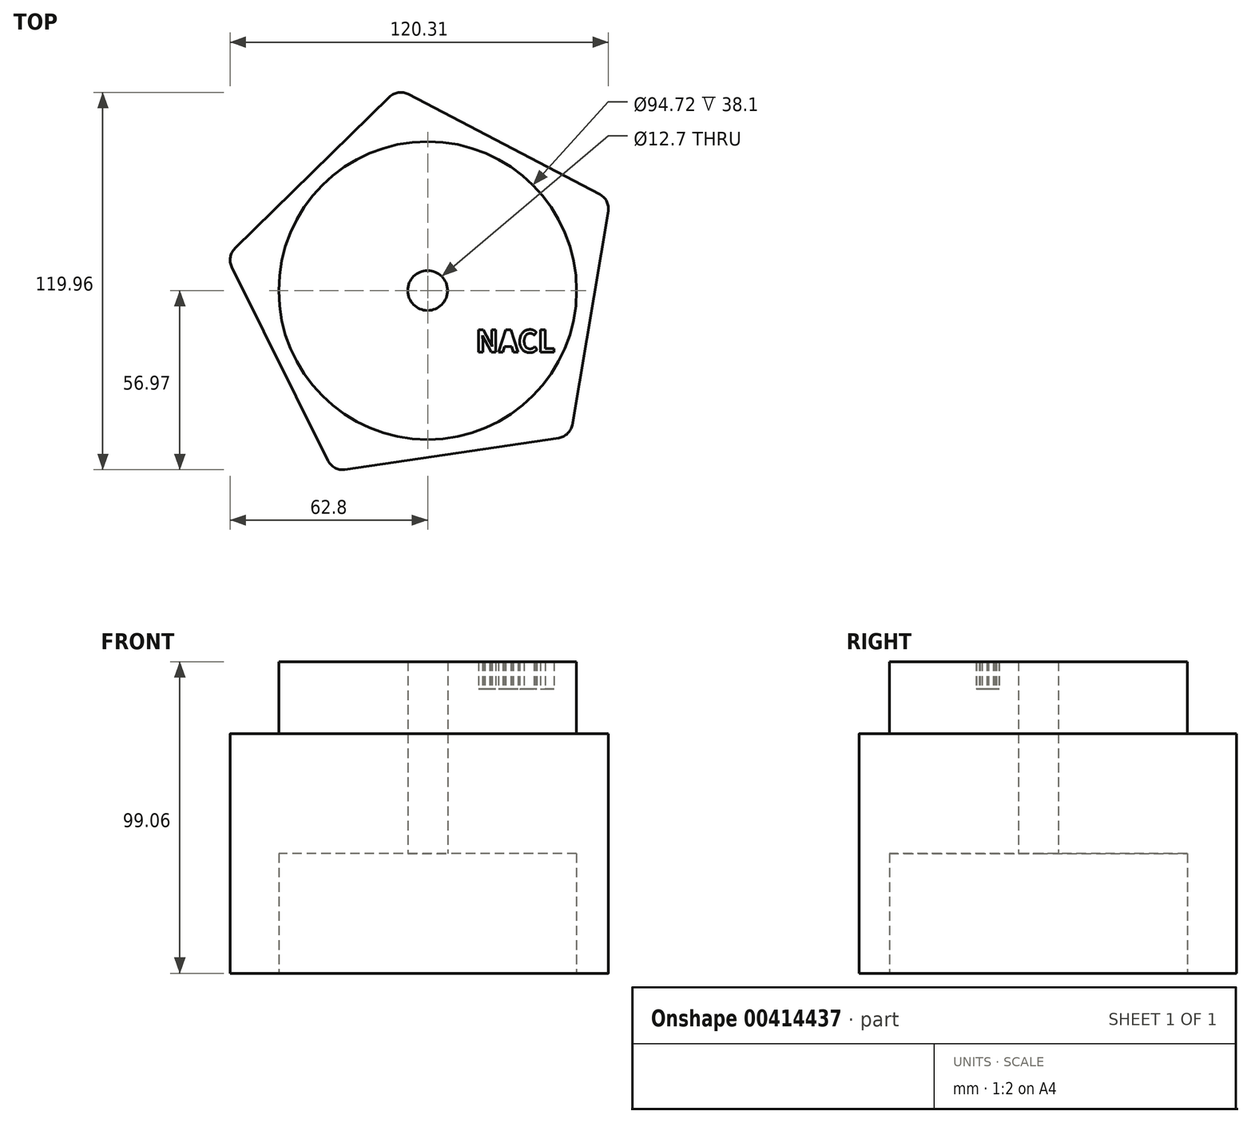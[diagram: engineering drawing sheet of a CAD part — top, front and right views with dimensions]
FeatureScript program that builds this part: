
annotation { "Feature Type Name" : "Feature", "Feature Type Description" : "" }
export const myFeature = defineFeature(function(context is Context, id is Id, definition is map)
    precondition{}
    {
        {
            var Q0;
            Q0=qCreatedBy(makeId("Top.planeOp"),FACE);
            var sketch = newSketch(context, id + "F0", { "sketchPlane" : qUnion([Q0])});
            skCircle(sketch, "E0.cCircle", {"center": v(0, 0) * mm, "radius": 64.82 * mm, "construction": true});
            skLineSegment(sketch, "E0.0", {"start": v(-9.5, 64.12) * mm, "end": v(58.05, 28.84) * mm});
            skLineSegment(sketch, "E0.1", {"start": v(58.05, 28.84) * mm, "end": v(45.37, -46.3) * mm});
            skLineSegment(sketch, "E0.2", {"start": v(45.37, -46.3) * mm, "end": v(-30.01, -57.45) * mm});
            skLineSegment(sketch, "E0.3", {"start": v(-30.01, -57.45) * mm, "end": v(-63.92, 10.79) * mm});
            skLineSegment(sketch, "E0.4", {"start": v(-63.92, 10.79) * mm, "end": v(-9.5, 64.12) * mm});
            skCircle(sketch, "E1", {"center": v(0, 0) * mm, "radius": 47.36 * mm});
            skSolve(sketch);
        }
        {
            var Q0;
            Q0=makeQuery(id+"F0.imprint","IMPRINT",FACE,{"disambiguationData":[TD([[makeQuery(id+"F0.imprint","IMPRINT",EDGE,{"derivedFrom":sQuery(id+"F0.wireOp",EDGE,"E1")}),1.0]])]});
            extrude(context, id + "F1", {"entities" : qUnion([Q0]), "depth" : 52.32 * mm});
        }
        {
            var Q0;
            Q0=makeQuery(id+"F0.imprint","IMPRINT",FACE,{"disambiguationData":[TD([[makeQuery(id+"F0.imprint","IMPRINT",EDGE,{"derivedFrom":sQuery(id+"F0.wireOp",EDGE,"E0.0")}),-1.0]])]});
            extrude(context, id + "F2", {"entities" : qUnion([Q0]), "operationType" : NewBodyOperationType.ADD, "endBound" : BoundingType.SYMMETRIC, "depth" : 76.2 * mm});
        }
        {
            var Q0;
            Q0=makeQuery(id+"F1.opExtrude","CAP_FACE",FACE,{"disambiguationData":[OSD([sQuery(id+"F0.wireOp",EDGE,"E1")])],"isStart":false});
            var sketch = newSketch(context, id + "F3", { "sketchPlane" : qUnion([Q0])});
            skText(sketch, "E2", { "text": "NACL", "fontName": "NotoSansCJKsc-Bold.otf"});
            const initialGuessF3  = {"E2": [0.01538, -0.01964, 1, 0, 0.00692]};
            skSetInitialGuess(sketch, initialGuessF3);
            skSolve(sketch);
        }
        {
            var Q0;
            Q0=makeQuery(id+"F3.imprint","IMPRINT",FACE,{"disambiguationData":[TD([[makeQuery(id+"F3.imprint","IMPRINT",EDGE,{"derivedFrom":sQuery(id+"F3.wireOp",EDGE,"E2.sketch_text.stroke-0")}),-1.0]])]});
            extrude(context, id + "F4", {"entities" : qUnion([Q0]), "operationType" : NewBodyOperationType.ADD, "endBound" : BoundingType.SYMMETRIC, "depth" : 17.27 * mm, "hasSecondDirection" : true, "secondDirectionOppositeDirection" : true, "secondDirectionDepth" : 25.4 * mm});
        }
        {
            var Q0;
            Q0=makeQuery(id+"F2.opExtrude","SWEPT_EDGE",EDGE,{"disambiguationData":[OSD([sQuery(id+"F0.wireOp",EDGE,"E0.2"),sQuery(id+"F0.wireOp",EDGE,"E0.3")])]});
            var Q1;
            Q1=makeQuery(id+"F2.opExtrude","SWEPT_EDGE",EDGE,{"disambiguationData":[OSD([sQuery(id+"F0.wireOp",EDGE,"E0.3"),sQuery(id+"F0.wireOp",EDGE,"E0.4")])]});
            var Q2;
            Q2=makeQuery(id+"F2.opExtrude","SWEPT_EDGE",EDGE,{"disambiguationData":[OSD([sQuery(id+"F0.wireOp",EDGE,"E0.0"),sQuery(id+"F0.wireOp",EDGE,"E0.4")])]});
            var Q3;
            Q3=makeQuery(id+"F2.opExtrude","SWEPT_EDGE",EDGE,{"disambiguationData":[OSD([sQuery(id+"F0.wireOp",EDGE,"E0.0"),sQuery(id+"F0.wireOp",EDGE,"E0.1")])]});
            var Q4;
            Q4=makeQuery(id+"F2.opExtrude","SWEPT_EDGE",EDGE,{"disambiguationData":[OSD([sQuery(id+"F0.wireOp",EDGE,"E0.1"),sQuery(id+"F0.wireOp",EDGE,"E0.2")])]});
            fillet(context, id + "F5", {"entities" : qUnion([Q0, Q1, Q2, Q3, Q4]), "radius" : 5.08 * mm, "tangentPropagation" : true, "allowEdgeOverflow" : false});
        }
        {
            var Q0;
            Q0=sQuery(id+"F0.wireOp",VERTEX,"E1.center");
            var Q1;
            Q1=makeQuery(id+"F1.opExtrude","SWEPT_BODY",BODY,{"disambiguationData":[OSD([sQuery(id+"F0.wireOp",EDGE,"E1")])]});
            hole(context, id + "F6", {"style" : HoleStyle.SIMPLE, "endStyle" : HoleEndStyle.THROUGH, "oppositeDirection" : true, "holeDiameter" : 12.7 * mm, "isTappedThrough" : true, "tappedDepth" : 12.7 * mm, "tapClearance" : 3, "startFromSketch" : true, "locations" : qUnion([Q0]), "scope" : qUnion([Q1])});
        }
        {
            var Q0;
            Q0 = qSketchRegion(id + "F3", true);
            extrude(context, id + "F7", {"entities" : qUnion([Q0]), "operationType" : NewBodyOperationType.ADD, "oppositeDirection" : true, "depth" : 1.78 * mm});
        }
    });
